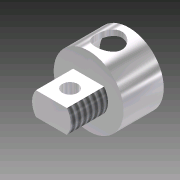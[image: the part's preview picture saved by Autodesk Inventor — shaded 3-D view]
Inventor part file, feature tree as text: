
AUTODESK INVENTOR PART (.ipt)
format: ipt  version: 2011 (Build 150239000, 239)  size: 123,392 bytes
history: native  units: in
note: dims shown in document units (in); Inventor stores cm internally (conversion verified against a paired STEP export)
features: extrude x5, sketch x5, thread x2, plane x1, projected_geometry x1
ambient origin geometry x8: Origin, YZ Plane, XZ Plane, XY Plane, X Axis, Y Axis, Z Axis, Center Point
bodies: Solid1 (feature_tree)
feature tree (14):
  extrude  "Extrusion1"  Depth=0.95in
  extrude  "Extrusion2"  Depth=0.1in TaperAngle=0.0deg
  extrude  "Extrusion3"  Depth=0.375in
  thread  "Thread1"  [1 undecoded]
  thread  "Thread2"  [1 undecoded]
  extrude  "Extrusion4"  Depth=1.0in TaperAngle=0.0deg
  plane  "Work Plane1"
  extrude  "Extrusion5"  Depth=0.25in
  sketch  "Sketch1"  dims[d0=1.125in d1=0.95in]
  sketch  "Sketch2"  dims[d2=0.55in d3=0.0in d4=0.1in d5=0.0in]
  sketch  "Sketch3"  dims[d6=0.625in d7=0.375in d8=0.0in d9=0.0in]
  sketch  "Sketch4"  dims[d10=0.6in d11=0.0in d12=1.0in d13=0.0in]
  sketch  "Sketch5"  dims[d14=1.0in d15=0.0in d16=0.25in d17=0.6in d18=0.0in d19=0.5625in d20=0.425in d21=0.6in d22=0.0in d23=0.325in d24=0.325in]
  projected_geometry  "Projected Loop1"
note: 2 required parameter values undecoded (feature->parameter linkage not recoverable at this tier; creation-order binding heuristic only, values carry confidence <= 0.55)
